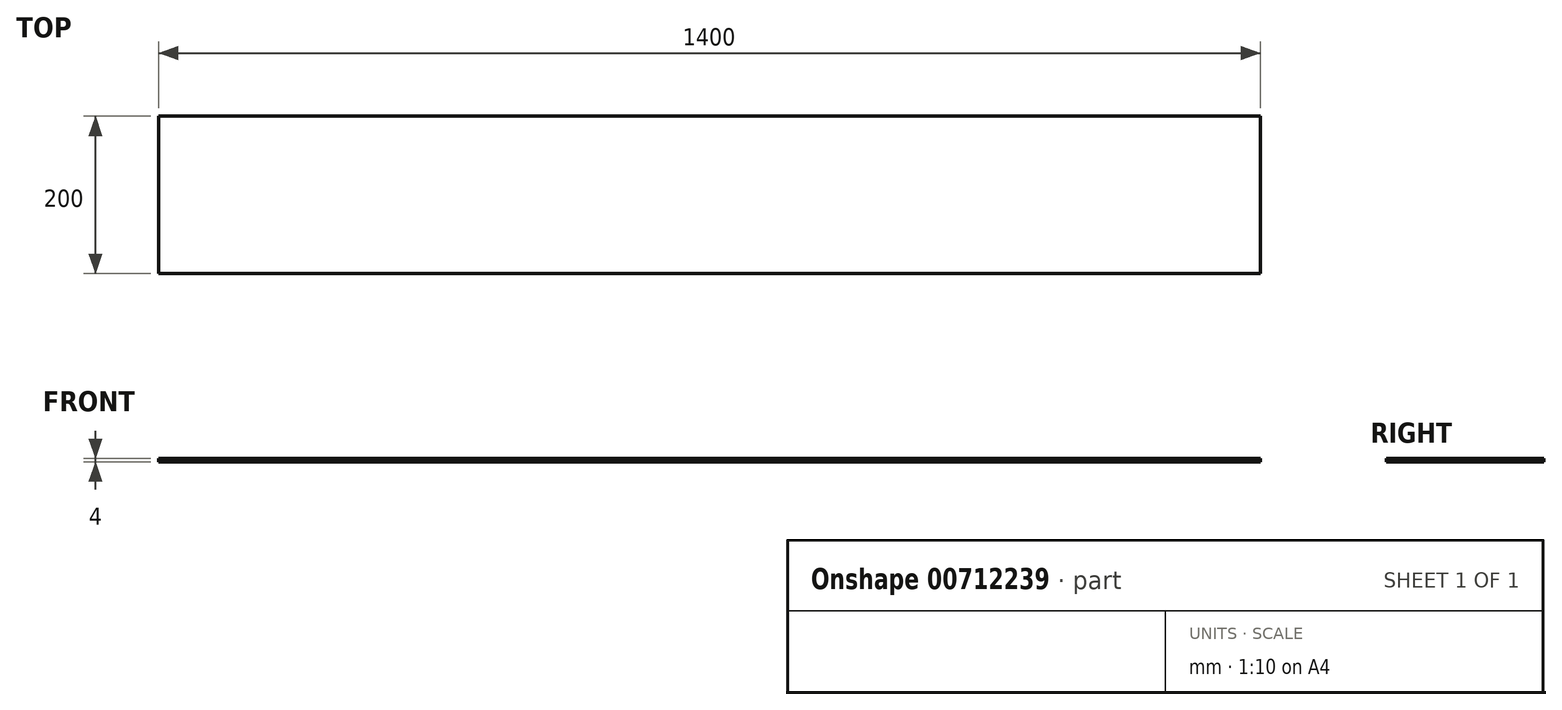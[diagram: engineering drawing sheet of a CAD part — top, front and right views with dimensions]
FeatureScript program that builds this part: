
annotation { "Feature Type Name" : "Feature", "Feature Type Description" : "" }
export const myFeature = defineFeature(function(context is Context, id is Id, definition is map)
    precondition{}
    {
        {
            var Q0;
            Q0=qCreatedBy(makeId("Top.planeOp"), FACE);
            var sketch = newSketch(context, id + "F0", { "sketchPlane" : qUnion([Q0])});
            skLineSegment(sketch, "E0.bottom", {"start": v(0, 0) * mm, "end": v(1400, 0) * mm});
            skLineSegment(sketch, "E0.top", {"start": v(0, 200) * mm, "end": v(1400, 200) * mm});
            skLineSegment(sketch, "E0.left", {"start": v(0, 0) * mm, "end": v(0, 200) * mm});
            skLineSegment(sketch, "E0.right", {"start": v(1400, 0) * mm, "end": v(1400, 200) * mm});
            skLineSegment(sketch, "E1", {"start": v(0, 100) * mm, "end": v(1400, 100) * mm, "construction": true});
            skLineSegment(sketch, "E2", {"start": v(100, 200) * mm, "end": v(100, 0) * mm, "construction": true});
            skLineSegment(sketch, "E3.1.0.0", {"start": v(200, 200) * mm, "end": v(200, 0) * mm, "construction": true});
            skLineSegment(sketch, "E3.2.0.0", {"start": v(300, 200) * mm, "end": v(300, 0) * mm, "construction": true});
            skLineSegment(sketch, "E3.3.0.0", {"start": v(400, 200) * mm, "end": v(400, 0) * mm, "construction": true});
            skLineSegment(sketch, "E3.4.0.0", {"start": v(500, 200) * mm, "end": v(500, 0) * mm, "construction": true});
            skLineSegment(sketch, "E3.5.0.0", {"start": v(600, 200) * mm, "end": v(600, 0) * mm, "construction": true});
            skLineSegment(sketch, "E3.6.0.0", {"start": v(700, 200) * mm, "end": v(700, 0) * mm, "construction": true});
            skLineSegment(sketch, "E3.7.0.0", {"start": v(800, 200) * mm, "end": v(800, 0) * mm, "construction": true});
            skLineSegment(sketch, "E3.8.0.0", {"start": v(900, 200) * mm, "end": v(900, 0) * mm, "construction": true});
            skLineSegment(sketch, "E3.9.0.0", {"start": v(1000, 200) * mm, "end": v(1000, 0) * mm, "construction": true});
            skLineSegment(sketch, "E3.10.0.0", {"start": v(1100, 200) * mm, "end": v(1100, 0) * mm, "construction": true});
            skLineSegment(sketch, "E3.11.0.0", {"start": v(1200, 200) * mm, "end": v(1200, 0) * mm, "construction": true});
            skLineSegment(sketch, "E3.12.0.0", {"start": v(1300, 200) * mm, "end": v(1300, 0) * mm, "construction": true});
            skLineSegment(sketch, "E3.direction1", {"start": v(100, 0) * mm, "end": v(200, 0) * mm, "construction": true});
            skSolve(sketch);
        }
        {
            var Q0;
            Q0 = qSketchRegion(id + "F0", true);
            extrude(context, id + "F1", {"entities" : qUnion([Q0]), "oppositeDirection" : true, "depth" : 4 * mm, "offsetDistance" : 25 * mm});
        }
    });
